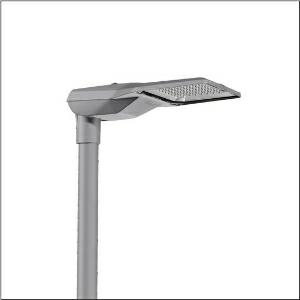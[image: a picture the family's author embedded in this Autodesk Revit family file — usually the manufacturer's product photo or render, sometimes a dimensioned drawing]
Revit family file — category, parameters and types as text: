
# Revit family: streetlight_sl_21_midi___st0_5a_5xe3b33s08mb_18c2
name_source: partatom
category: Lighting Fixtures
units: mm (PartAtom-declared; Revit-internal decimal feet)

## family parameters
Cut with Voids When Loaded = No
Host = Face
Light Source = No
Part Type = Normal
Room Calculation Point = No
Round Connector Dimension = Use Diameter
Shared = No

## types (1)
- --- (1 x LED, 18270 lm, 136 W, 3000K)
    Apparent Load = 136 VA
    CIE Flux Codes = 41 75 97 100 100
    Color Rendering = 70
    Color Temperature = 3000K
    Default Elevation = 1800 mm
    Description = Streetlight SL 21 midi, mast luminaire, primary light control with lens, of PMMA, primary optical cover: cover, of toughened safety glass, transparent, light distribution: ST0.5a, light emission: direct distribution, primary light characteristic: asymmetric, installation type: side-entry, post-top, LED, High Power LED, rated luminous flux: 18.270lm, luminous efficacy: 134lm/W, light colour: 730, colour temperature: 3000K, control gear: D4i, control: overheat protection, constant luminous flux control, time-dependent luminous flux control, flexible luminous flux parameterisation, pre-setting: logarithmic dimming characteristic, mains connection: 230..240V, AC, 50/60Hz, start of lifetime: 136W, end of service life: 142W, reduction: 61W, luminaire housing, of diecast aluminium, powder-coated, SITECO metallic grey (DB 702S), corrosivity category C5 high according to DIN EN ISO 12944, please order mast flange separately, inclination adjustable: 0°, 5°, 10°, 15°, sealing non-destructively replaceable, multi-level sealing system, length: 644mm, width: 335mm, height: 110mm, mast flange for spigot size: 42mm (side-entry): 5XC10008XM4, 60/48mm (side-entry/post-top): 5XC10108XM2, 76/60mm (side-entry/post-top): 5XC10108XM1, mounting height: 4..8m, Smart Interface above, protection rating (complete): IP66, insulation class (complete): insulation class II (safety insulation), certification: CE, ENEC, ENEC+, VDE, impact resistance: IK10, permissible operating ambient temperature for outdoor applications: -40..+50°C, standard-compliant lighting for roads and squares, packaging unit: 1 piece

Light Distribution: ST0.5a
    Height = 111 mm
    Lamp = 1 x LED
    Lamp Light Flux = 18270 lm
    Lamp Power = 136 W
    Lamp count = 1
    Length = 644 mm
    Luminous efficacy = 134 lm/W
    Manufacturer = Siteco
    ModVariant = No
    Model = 5XE3B33S08MB
    Number of Poles = 1
    OnlyDefault = Yes
    Power Factor = 1
    Product Name = Streetlight SL 21 midi | ST0.5a
    Product group = mast luminaire | pylon top
    ProductGroupID = 6100
    Protection Class = Protection class II
    Protection Degree = IP 66
    RLX_Detail_Level = 1
    RLX_Emergency_Light_Flux = 0 lm
    RLX_Emergency_Type = 0
    RLX_Emergency_Type_DB = No
    RlxData = <blob elided: 37865 chars, md5=778b02f6>
    Socket = socket
    Standby Power = 0 W
    System Light Flux = 18270 lm
    System Power = 136 W
    Type Comments = factory setting: luminous flux: 100 % | dim-lin: 254 | 695 mA
    Type Image = l_1004302.jpg
    URL = http://relux.com
    VarID = @adj_189185
    Voltage = 0 V
    Weight = 0.00 kg
    Width = 336 mm

## geometry (parser evidence)
native form markers: Blend x4, Sweep x11
no freeform markers — native parametric forms only
